# Revit family: НЕВАТОМ_Вентилятор VKP, версия 1
name_source: partatom
category: Оборудование
revit_build: Autodesk Revit 2017 (Build: 20170118_1100(x64)
units: mm (PartAtom-declared; Revit-internal decimal feet)

## family parameters
Всегда вертикально = Да
На основе рабочей плоскости = Нет
Общий = Нет
При загрузке вырезать с полостями = Нет
Размер круглого соединителя = Использовать диаметр
Тип детали = Вставляется
Точка расчета площади = Нет

## types (13) — shared parameters
ADSK_Единица измерения = шт.
ADSK_Завод-изготовитель = НЕВАТОМ
ADSK_Количество = 1
ADSK_Материал наименование = Оцинкованная сталь
ADSK_Наименование = Вентилятор канальный прямоугольный с вперед загнутыми лопатками
Nevatom_URL = https://t.me
Ключевая пометка = Вентиляция
Материал = Сталь серая
крышка = СВМПЭ, белый

## per-type parameters (varying)
| type | A | ADSK_Масса | ADSK_Масса_Текст | ADSK_Напряжение | ADSK_Полная мощность | ADSK_Размер_Высота | ADSK_Размер_Длина | ADSK_Размер_Ширина | ADSK_Ток | ADSK_Частота вращения вентилятора | B | E | F | H | L | d1 | d2 | Макс. расход воздуха | Полное давление |
| VKP 400-200/20-4E | 400 мм | 10 | 10 | 230 В | 0 кВт | 240 мм | 440 мм | 505 мм | 2 А | 1280 | 200 мм | 440 мм | 240 мм | 265 мм | 505 мм | 260 мм | 130 мм | 1200.0 м³/ч | 240.0 Па |
| VKP 400-200/20-4D | 400 мм | 12 | 12 | 380 В | 0 кВт | 240 мм | 440 мм | 505 мм | 1 А | 1270 | 200 мм | 440 мм | 240 мм | 265 мм | 505 мм | 260 мм | 130 мм | 1200.0 м³/ч | 255.0 Па |
| VKP 500-250/22-4E | 500 мм | 18 | 18 | 230 В | 1 кВт | 290 мм | 540 мм | 550 мм | 2 А | 1320 | 250 мм | 540 мм | 290 мм | 315 мм | 550 мм | 325 мм | 163 мм | 1600.0 м³/ч | 300.0 Па |
| VKP 500-250/22-4D | 500 мм | 18 | 18 | 380 В | 0 кВт | 290 мм | 540 мм | 550 мм | 1 А | 1300 | 250 мм | 540 мм | 290 мм | 315 мм | 550 мм | 325 мм | 163 мм | 1800.0 м³/ч | 310.0 Па |
| VKP 500-300/25-4E | 500 мм | 21 | 21 | 230 В | 1 кВт | 340 мм | 540 мм | 570 мм | 4 А | 1330 | 300 мм | 540 мм | 340 мм | 365 мм | 570 мм | 325 мм | 163 мм | 2700.0 м³/ч | 380.0 Па |
| VKP 500-300/25-4D | 500 мм | 29 | 29 | 380 В | 1 кВт | 340 мм | 540 мм | 570 мм | 2 А | 1400 | 300 мм | 540 мм | 340 мм | 365 мм | 570 мм | 325 мм | 163 мм | 2950.0 м³/ч | 410.0 Па |
| VKP 600-300/28-4E | 600 мм | 28 | 28 | 230 В | 2 кВт | 340 мм | 640 мм | 640 мм | 7 А | 1360 | 300 мм | 640 мм | 340 мм | 365 мм | 640 мм | 390 мм | 195 мм | 2700.0 м³/ч | 410.0 Па |
| VKP 600-300/28-4D | 600 мм | 32 | 32 | 380 В | 2 кВт | 340 мм | 640 мм | 640 мм | 3 А | 1360 | 300 мм | 640 мм | 340 мм | 365 мм | 640 мм | 390 мм | 195 мм | 3500.0 м³/ч | 450.0 Па |
| VKP 600-350/31-4D | 600 мм | 38 | 38 | 380 В | 2 кВт | 390 мм | 640 мм | 680 мм | 4 А | 1360 | 350 мм | 640 мм | 390 мм | 415 мм | 680 мм | 390 мм | 195 мм | 4200.0 м³/ч | 631.0 Па |
| VKP 700-400/35-4D | 700 мм | 60 | 60 | 380 В | 4 кВт | 440 мм | 740 мм | 745 мм | 6 А | 1340 | 400 мм | 740 мм | 440 мм | 475 мм | 745 мм | 455 мм | 228 мм | 5600.0 м³/ч | 760.0 Па |
| VKP 800-500/40-4D | 800 мм | 75 | 75 | 380 В | 5 кВт | 560 мм | 860 мм | 815 мм | 8 А | 1400 | 500 мм | 860 мм | 560 мм | 575 мм | 815 мм | 520 мм | 260 мм | 6500.0 м³/ч | 1000.0 Па |
| VKP 900-500/45-6D | 900 мм | 80 | 80 | 380 В | 4 кВт | 560 мм | 960 мм | 905 мм | 6 А | 930 | 500 мм | 960 мм | 560 мм | 575 мм | 905 мм | 585 мм | 293 мм | 7500.0 м³/ч | 695.0 Па |
| VKP 1000-500/50-6D | 1000 мм | 98 | 98 | 380 В | 4 кВт | 560 мм | 1060 мм | 905 мм | 8 А | 900 | 500 мм | 1060 мм | 560 мм | 575 мм | 905 мм | 650 мм | 325 мм | 8500.0 м³/ч | 900.0 Па |

note: column(s) folded — value = type name in every type: ADSK_Марка
